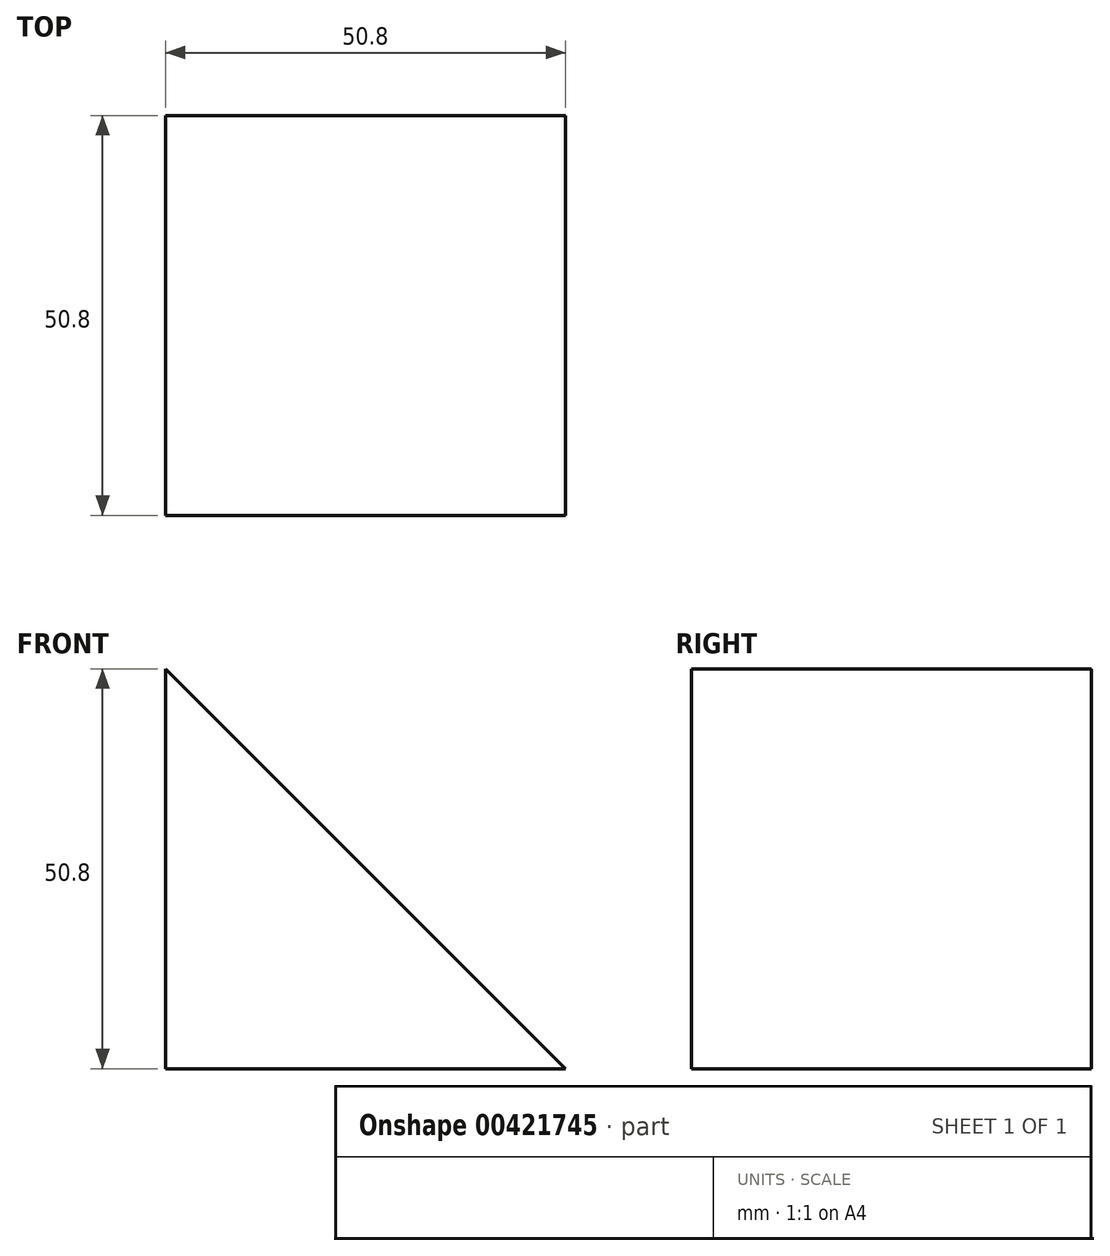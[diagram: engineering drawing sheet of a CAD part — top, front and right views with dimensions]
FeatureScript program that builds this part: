
annotation { "Feature Type Name" : "Feature", "Feature Type Description" : "" }
export const myFeature = defineFeature(function(context is Context, id is Id, definition is map)
    precondition{}
    {
        {
            var Q0;
            Q0=qCreatedBy(makeId("Front.planeOp"),FACE);
            var sketch = newSketch(context, id + "F0", { "sketchPlane" : qUnion([Q0])});
            skLineSegment(sketch, "E0", {"start": v(0, 0) * mm, "end": v(-50.8, 0) * mm});
            skLineSegment(sketch, "E1", {"start": v(-50.8, 50.8) * mm, "end": v(-50.8, 0) * mm});
            skLineSegment(sketch, "E2", {"start": v(-50.8, 50.8) * mm, "end": v(0, 0) * mm});
            skSolve(sketch);
        }
        {
            var Q0;
            Q0=makeQuery(id+"F0.imprint","IMPRINT",FACE,{"disambiguationData":[TD([[makeQuery(id+"F0.imprint","IMPRINT",EDGE,{"derivedFrom":sQuery(id+"F0.wireOp",EDGE,"E0")}),-1.0]])]});
            extrude(context, id + "F1", {"entities" : qUnion([Q0]), "depth" : 50.8 * mm});
        }
    });
